# Revit family: Plumbing Fixture-Grease_Interseptor_Mifab_MI-SD
name_source: partatom
category: Plumbing Fixtures
revit_build: Autodesk Revit Structure 2013 (Build: 20120221_2030(x64)
units: mm (PartAtom-declared; Revit-internal decimal feet)

## types (10) — shared parameters
Assembly Code = D2090300
Description = Sediment Drain Interceptor
Interceptor Material = Acid Resistant Epoxy Coated Green
Manufacturer = MIFAB
URL = www.mifab.com
zero-valued in all types: Default Elevation, WFU

## per-type parameters (varying)
| type | A | B | C | D | E | F | Standard Inlet And Outlet Radii | Water Capacity |
| MI-SD-1 | 12 " | 14 " | 4.5 " | 10.5 " | 15 " | 2 " | 1 " | 12 Gallons |
| MI-SD-2 | 16 " | 20.75 " | 7.5 " | 12.5 " | 20 " | 3 " | 1.5 " | 23 Gallons |
| MI-SD-3 | 20.5 " | 27 " | 7.625 " | 17.625 " | 25.25 " | 3 " | 1.5 " | 77 Gallons |
| MI-SD-4 | 20.5 " | 27 " | 10 " | 23 " | 33 " | 3 " | 1.5 " | 105 Gallons |
| MI-SD-5 | 24.375 " | 24.5 " | 10 " | 22 " | 32 " | 3 " | 1.5 " | 193 Gallons |
| MI-SD-6 | 48.625 " | 24.5 " | 10 " | 22 " | 32 " | 3 " | 1.5 " | 350 Gallons |
| MI-SD-7 | 48.625 " | 30.5 " | 11 " | 27 " | 38 " | 4 " | 2 " | 438 Gallons |
| MI-SD-8 | 60.5 " | 36.5 " | 11 " | 27 " | 38 " | 4 " | 2 " | 665 Gallons |
| MI-SD-9 | 72.625 " | 36.5 " | 11 " | 27 " | 38 " | 4 " | 2 " | 910 Gallons |
| MI-SD-10 | 96.625 " | 36.5 " | 15 " | 29 " | 44 " | 4 " | 2 " | 1155 Gallons |

note: column(s) folded — value = type name in every type: Model

## geometry (parser evidence)
native form markers: Blend x4, Sweep x1
no freeform markers — native parametric forms only
